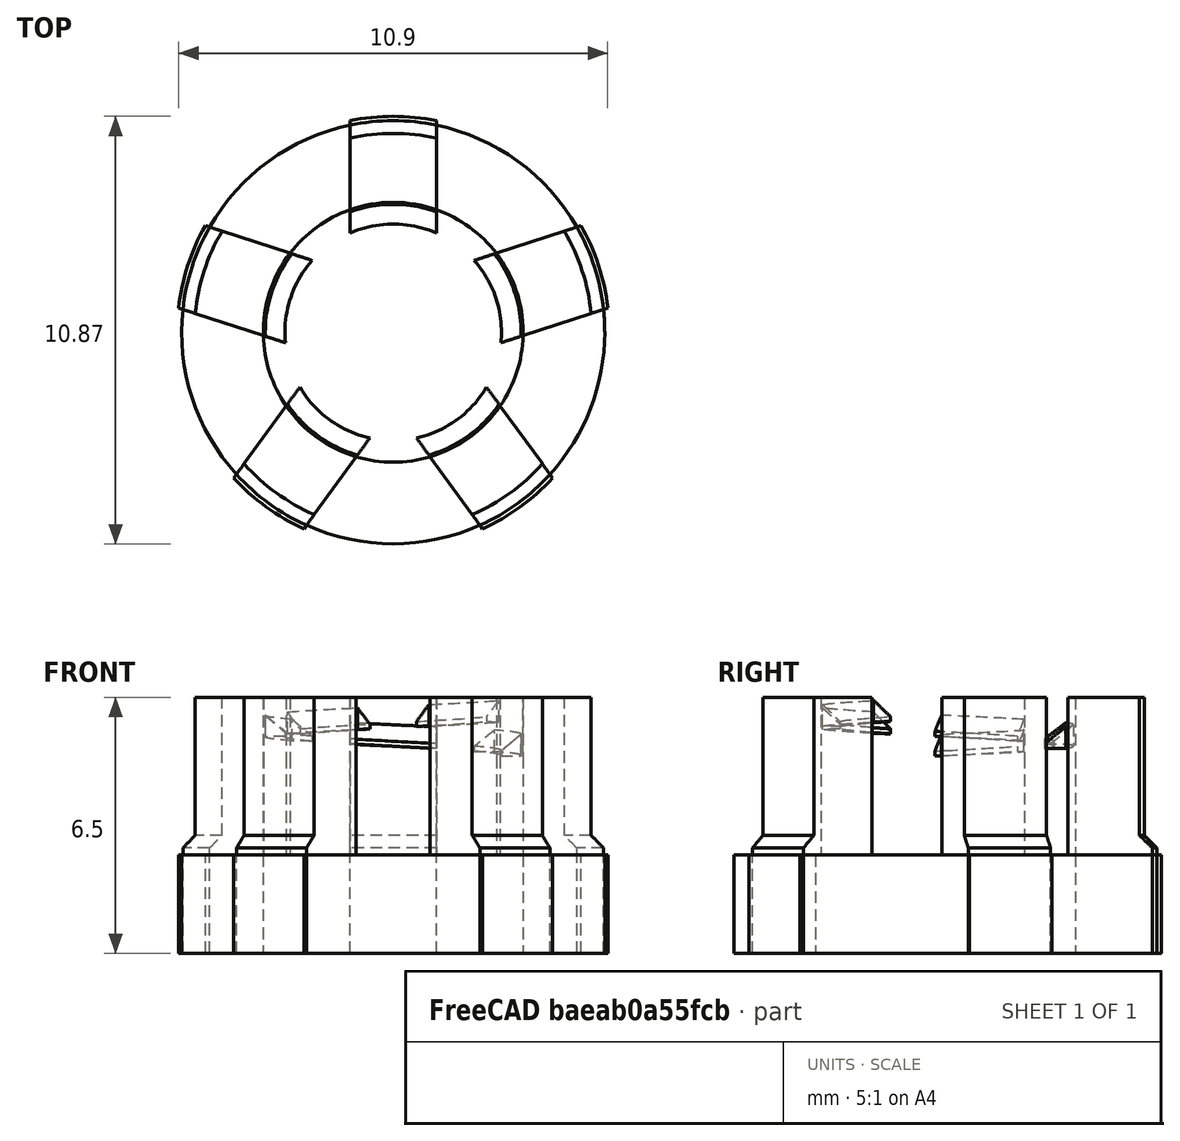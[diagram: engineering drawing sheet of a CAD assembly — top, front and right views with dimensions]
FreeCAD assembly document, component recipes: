
FREECAD ASSEMBLY — COMPONENT RECIPES ("drivers interworm")

This assembly document has 9 components, labeled P0..P8 below (a component is one placed body or linked part). 1 of them carries a construction recipe — the FreeCAD feature program that regenerates the part from scratch, quoted from this document or its linked companion documents; the rest are supplied as boundary geometry only. No exploded tour is included for this assembly.
COMPONENT P0 — recipe-attached ("Body", modeled in this document).
Construction recipe (the document's own serialized feature program — sketch geometry with constraints, then the solid features built on it; lengths are millimeters unless a unit is written):

FEATURE [Sketcher::SketchObject] Sketch002
  FullyConstrained = true
  MapMode = 5
  Placement = pos=(0,0,0) rot=(1,0,0;1.5708rad)
  Support = -> [XZ_Plane]
  sketch-geometry (3):
    g0: LineSegment StartX=3.25 StartY=0 StartZ=0 EndX=2.6 EndY=0 EndZ=0
    g1: LineSegment StartX=2.6 StartY=0 StartZ=0 EndX=3.25 EndY=0.545415 EndZ=0
    g2: LineSegment StartX=3.25 StartY=0 StartZ=0 EndX=3.25 EndY=0.545415 EndZ=0
  constraints (9):
    c: PointOnObject(g0,g-1)
    c: PointOnObject(g0,g-1)
    c: Coincident(g1,g0)
    c: Coincident(g2,g0)
    c: Coincident(g2,g1)
    c: Vertical(g2)
    c: DistanceX(g0,g0) = 0.65
    c: Angle(g1) = 0.698132
    c: DistanceX(g-1,g1) = 3.25
FEATURE [PartDesign::AdditiveHelix] AdditiveHelix
  Angle = 0
  Axis = (0,2e-16,1)
  Base = (0,0,0)
  Growth = 0
  HasBeenEdited = true
  Height = 0.943
  LeftHanded = false
  Mode = 0
  Outside = false
  Pitch = 0.943
  Placement = pos=(0,0,0) rot=(1,0,0;1.5708rad)
  Profile = -> Sketch002
  ReferenceAxis = -> Sketch002 [V_Axis]
  Turns = 1
  expr: Height = 0.943 mm * 1
FEATURE [PartDesign::Body] Body
  Group = -> [Sketch002,AdditiveHelix]
  Origin = -> Origin
  Placement = pos=(0,0,5) rot=(0,0,1;-0.174533rad)
  Tip = -> AdditiveHelix
COMPONENT P1 — geometry summary ("Cutout 2"; no construction recipe available for this part):
  bounding box: 7.5 x 5.8 x 3.8 mm
  tessellated surface: 48 triangles
  volume: 90 mm^3 (55% of its bounding box)
  symmetry: mirror-symmetric across its z mid-plane
COMPONENT P2 — geometry summary ("Cutout 3"; no construction recipe available for this part):
  bounding box: 7.5 x 5.6 x 4.9 mm
  tessellated surface: 48 triangles
  volume: 90 mm^3 (43% of its bounding box)
  symmetry: mirror-symmetric across its z mid-plane
COMPONENT P3 — geometry summary ("Cutout 4"; no construction recipe available for this part):
  bounding box: 7.5 x 5.6 x 4.9 mm
  tessellated surface: 48 triangles
  volume: 90 mm^3 (43% of its bounding box)
  symmetry: mirror-symmetric across its z mid-plane
COMPONENT P4 — geometry summary ("Cutout 5"; no construction recipe available for this part):
  bounding box: 7.5 x 5.8 x 3.8 mm
  tessellated surface: 48 triangles
  volume: 90 mm^3 (55% of its bounding box)
  symmetry: mirror-symmetric across its z mid-plane
COMPONENT P5 — geometry summary ("Locking Lug 002"; no construction recipe available for this part):
  bounding box: 5.8 x 3.8 x 2.5 mm
  tessellated surface: 48 triangles
  volume: 30 mm^3 (55% of its bounding box)
COMPONENT P6 — geometry summary ("Locking Lug 003"; no construction recipe available for this part):
  bounding box: 5.6 x 4.9 x 2.5 mm
  tessellated surface: 48 triangles
  volume: 30 mm^3 (43% of its bounding box)
COMPONENT P7 — geometry summary ("Locking Lug 004"; no construction recipe available for this part):
  bounding box: 5.6 x 4.9 x 2.5 mm
  tessellated surface: 48 triangles
  volume: 30 mm^3 (43% of its bounding box)
COMPONENT P8 — geometry summary ("Locking Lug 005"; no construction recipe available for this part):
  bounding box: 5.8 x 3.8 x 2.5 mm
  tessellated surface: 48 triangles
  volume: 30 mm^3 (55% of its bounding box)
PROVENANCE & LICENSES
A FreeCAD (.FCStd) document from a public repository crawl; recipes are the document's own serialized feature recipes (and, for linked parts, companion documents' recipes).
License: as declared in the source repository (recorded in the dataset sidecar).
